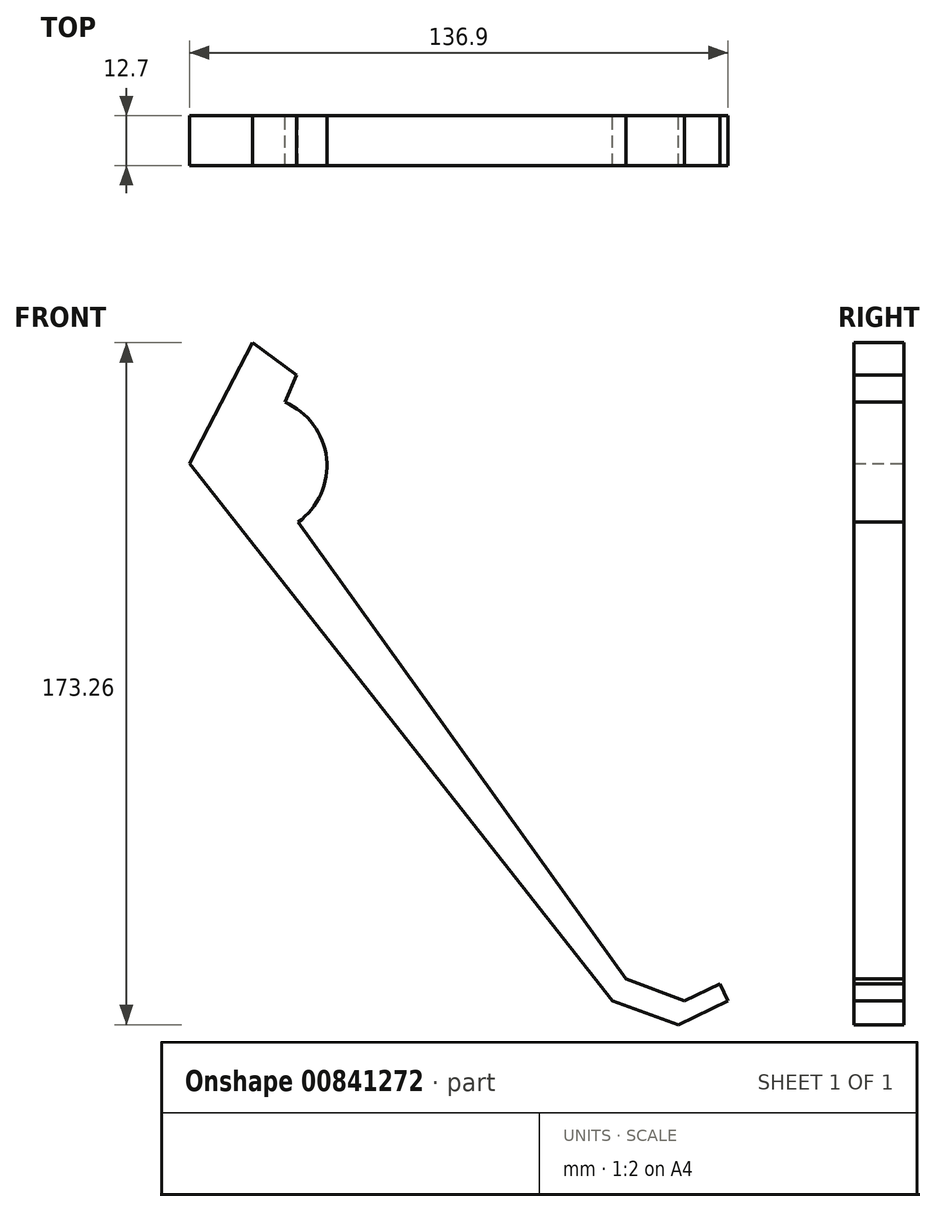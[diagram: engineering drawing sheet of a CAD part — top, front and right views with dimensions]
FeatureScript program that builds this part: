
annotation { "Feature Type Name" : "Feature", "Feature Type Description" : "" }
export const myFeature = defineFeature(function(context is Context, id is Id, definition is map)
    precondition{}
    {
        {
            var Q0;
            Q0=qCreatedBy(makeId("Front.planeOp"),FACE);
            var sketch = newSketch(context, id + "F0", { "sketchPlane" : qUnion([Q0])});
            skLineSegment(sketch, "E0", {"start": v(-43.16, 54.54) * mm, "end": v(-59.28, 23.87) * mm});
            skLineSegment(sketch, "E1", {"start": v(-59.28, 23.87) * mm, "end": v(48.22, -112.71) * mm});
            skLineSegment(sketch, "E2", {"start": v(48.22, -112.71) * mm, "end": v(64.97, -118.72) * mm});
            skLineSegment(sketch, "E3", {"start": v(64.97, -118.72) * mm, "end": v(77.62, -112.71) * mm});
            skLineSegment(sketch, "E4", {"start": v(77.62, -112.71) * mm, "end": v(75.57, -108.4) * mm});
            skLineSegment(sketch, "E5", {"start": v(75.57, -108.4) * mm, "end": v(66.47, -112.71) * mm});
            skLineSegment(sketch, "E6", {"start": v(66.47, -112.71) * mm, "end": v(51.7, -107.02) * mm});
            skLineSegment(sketch, "E7", {"start": v(51.7, -107.02) * mm, "end": v(-31.63, 8.96) * mm});
            skLineSegment(sketch, "E8", {"start": v(-35.02, 39.42) * mm, "end": v(-32.1, 46.32) * mm});
            skLineSegment(sketch, "E9", {"start": v(-32.1, 46.32) * mm, "end": v(-43.16, 54.54) * mm});
            skArc(sketch, "E10", {"start": v(-31.63, 8.96) * mm, "mid": v(-24.42, 25.18) * mm, "end": v(-35.02, 39.42) * mm});
            skSolve(sketch);
        }
        {
            var Q0;
            Q0 = qSketchRegion(id + "F0", true);
            extrude(context, id + "F1", {"entities" : qUnion([Q0]), "depth" : 12.7 * mm, "offsetDistance" : 25.4 * mm});
        }
    });
